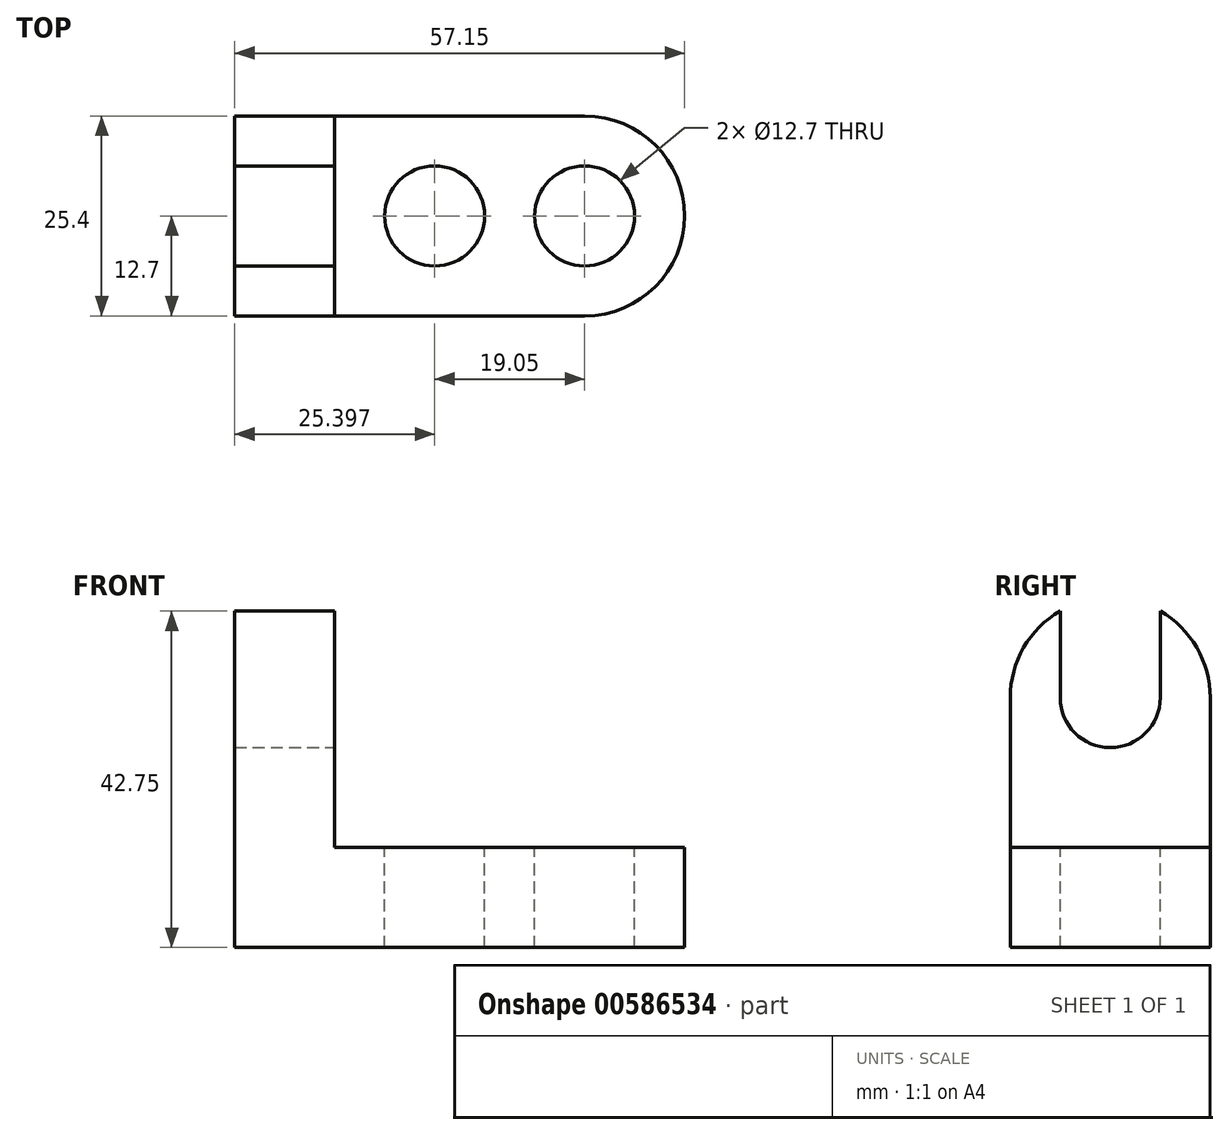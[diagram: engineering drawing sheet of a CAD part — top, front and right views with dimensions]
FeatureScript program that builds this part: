
annotation { "Feature Type Name" : "Feature", "Feature Type Description" : "" }
export const myFeature = defineFeature(function(context is Context, id is Id, definition is map)
    precondition{}
    {
        {
            var Q0;
            Q0=qCreatedBy(makeId("Front.planeOp"),FACE);
            var sketch = newSketch(context, id + "F0", { "sketchPlane" : qUnion([Q0])});
            skLineSegment(sketch, "E0", {"start": v(-66.14, 48.6) * mm, "end": v(-66.14, -2.2) * mm});
            skLineSegment(sketch, "E1", {"start": v(-66.14, -2.2) * mm, "end": v(-9, -2.2) * mm});
            skLineSegment(sketch, "E2", {"start": v(-9, -2.2) * mm, "end": v(-9, 10.5) * mm});
            skLineSegment(sketch, "E3", {"start": v(-9, 10.5) * mm, "end": v(-53.44, 10.5) * mm});
            skLineSegment(sketch, "E4", {"start": v(-53.44, 10.5) * mm, "end": v(-53.44, 48.6) * mm});
            skLineSegment(sketch, "E5", {"start": v(-53.44, 48.6) * mm, "end": v(-66.14, 48.6) * mm});
            skSolve(sketch);
        }
        {
            var Q0;
            Q0 = qSketchRegion(id + "F0", true);
            extrude(context, id + "F1", {"entities" : qUnion([Q0]), "depth" : 25.4 * mm, "offsetDistance" : 25.4 * mm});
        }
        {
            var Q0;
            Q0=makeQuery(id+"F1.opExtrude","SWEPT_FACE",FACE,{"disambiguationData":[OSD([sQuery(id+"F0.wireOp",EDGE,"E4")])]});
            var sketch = newSketch(context, id + "F2", { "sketchPlane" : qUnion([Q0])});
            skArc(sketch, "E6", {"start": v(0, 35.9) * mm, "mid": v(-12.7, 48.6) * mm, "end": v(-25.4, 35.9) * mm});
            skSolve(sketch);
        }
        {
            var Q0;
            Q0 = qSketchRegion(id + "F2", true);
            var Q1;
            {var subQ0=sQuery(id+"F2.wireOp",EDGE,"E6");var subQ1=sQuery(id+"F0.wireOp",EDGE,"E4");var subQ2=makeQuery(id+"F1.opExtrude","CAP_EDGE",EDGE,{"disambiguationData":[OSD([subQ1])],"isStart":false});var subQ3=makeQuery(id+"F2.imprint","INTERSECT",VERTEX,{"derivedFrom":[subQ2,subQ0]});Q1=makeQuery(id+"F2.imprint","IMPRINT",FACE,{"disambiguationData":[TD([[makeQuery(id+"F2.imprint","IMPRINT",EDGE,{"disambiguationData":[TD([[subQ3,1.0]])],"derivedFrom":subQ0}),-1.0]])]});}
            var Q2;
            {var subQ0=sQuery(id+"F2.wireOp",EDGE,"E6");var subQ1=sQuery(id+"F0.wireOp",EDGE,"E4");var subQ2=makeQuery(id+"F1.opExtrude","CAP_EDGE",EDGE,{"disambiguationData":[OSD([subQ1])],"isStart":true});var subQ3=makeQuery(id+"F2.imprint","INTERSECT",VERTEX,{"derivedFrom":[subQ2,subQ0]});Q2=makeQuery(id+"F2.imprint","IMPRINT",FACE,{"disambiguationData":[TD([[makeQuery(id+"F2.imprint","IMPRINT",EDGE,{"disambiguationData":[TD([[subQ3,-1.0]])],"derivedFrom":subQ0}),-1.0]])]});}
            extrude(context, id + "F3", {"entities" : qUnion([Q0, Q1, Q2]), "operationType" : NewBodyOperationType.REMOVE, "oppositeDirection" : true, "depth" : 25.4 * mm, "offsetDistance" : 25.4 * mm});
        }
        {
            var Q0;
            Q0=makeQuery(id+"F1.opExtrude","SWEPT_FACE",FACE,{"disambiguationData":[OSD([sQuery(id+"F0.wireOp",EDGE,"E4")])]});
            var sketch = newSketch(context, id + "F4", { "sketchPlane" : qUnion([Q0])});
            skArc(sketch, "E7", {"start": v(-19.05, 29.55) * mm, "mid": v(-12.7, 23.2) * mm, "end": v(-6.35, 29.55) * mm});
            skLineSegment(sketch, "E8", {"start": v(-19.05, 29.55) * mm, "end": v(-19.05, 46.9) * mm});
            skLineSegment(sketch, "E9", {"start": v(-6.35, 29.55) * mm, "end": v(-6.35, 46.9) * mm});
            skSolve(sketch);
        }
        {
            var Q0;
            Q0 = qSketchRegion(id + "F4", true);
            var Q1;
            Q1=makeQuery(id+"F4.imprint","IMPRINT",FACE,{"disambiguationData":[TD([[makeQuery(id+"F4.imprint","IMPRINT",EDGE,{"derivedFrom":sQuery(id+"F4.wireOp",EDGE,"E7")}),1.0]])]});
            extrude(context, id + "F5", {"entities" : qUnion([Q0, Q1]), "operationType" : NewBodyOperationType.REMOVE, "oppositeDirection" : true, "depth" : 25.4 * mm, "offsetDistance" : 25.4 * mm});
        }
        {
            var Q0;
            Q0=makeQuery(id+"F1.opExtrude","SWEPT_FACE",FACE,{"disambiguationData":[OSD([sQuery(id+"F0.wireOp",EDGE,"E3")])]});
            var sketch = newSketch(context, id + "F6", { "sketchPlane" : qUnion([Q0])});
            skCircle(sketch, "E10", {"center": v(-21.7, -12.7) * mm, "radius": 6.35 * mm});
            skCircle(sketch, "E11", {"center": v(-40.74, -12.7) * mm, "radius": 6.35 * mm});
            skSolve(sketch);
        }
        {
            var Q0;
            Q0 = qSketchRegion(id + "F6", true);
            extrude(context, id + "F7", {"entities" : qUnion([Q0]), "operationType" : NewBodyOperationType.REMOVE, "oppositeDirection" : true, "depth" : 25.4 * mm, "offsetDistance" : 25.4 * mm});
        }
        {
            var Q0;
            Q0=makeQuery(id+"F1.opExtrude","SWEPT_FACE",FACE,{"disambiguationData":[OSD([sQuery(id+"F0.wireOp",EDGE,"E3")])]});
            var sketch = newSketch(context, id + "F8", { "sketchPlane" : qUnion([Q0])});
            skArc(sketch, "E12", {"start": v(-21.7, -25.4) * mm, "mid": v(-9, -12.7) * mm, "end": v(-21.7, 0) * mm});
            skSolve(sketch);
        }
        {
            var Q0;
            Q0 = qSketchRegion(id + "F8", true);
            var Q1;
            {var subQ0=sQuery(id+"F8.wireOp",EDGE,"E12");var subQ1=sQuery(id+"F0.wireOp",EDGE,"E3");var subQ2=makeQuery(id+"F1.opExtrude","CAP_EDGE",EDGE,{"disambiguationData":[OSD([subQ1])],"isStart":true});var subQ3=makeQuery(id+"F8.imprint","INTERSECT",VERTEX,{"derivedFrom":[subQ2,subQ0]});Q1=makeQuery(id+"F8.imprint","IMPRINT",FACE,{"disambiguationData":[TD([[makeQuery(id+"F8.imprint","IMPRINT",EDGE,{"disambiguationData":[TD([[subQ3,1.0]])],"derivedFrom":subQ0}),-1.0]])]});}
            var Q2;
            {var subQ0=sQuery(id+"F8.wireOp",EDGE,"E12");var subQ1=sQuery(id+"F0.wireOp",EDGE,"E3");var subQ2=makeQuery(id+"F1.opExtrude","CAP_EDGE",EDGE,{"disambiguationData":[OSD([subQ1])],"isStart":false});var subQ3=makeQuery(id+"F8.imprint","INTERSECT",VERTEX,{"derivedFrom":[subQ2,subQ0]});Q2=makeQuery(id+"F8.imprint","IMPRINT",FACE,{"disambiguationData":[TD([[makeQuery(id+"F8.imprint","IMPRINT",EDGE,{"disambiguationData":[TD([[subQ3,-1.0]])],"derivedFrom":subQ0}),-1.0]])]});}
            extrude(context, id + "F9", {"entities" : qUnion([Q0, Q1, Q2]), "operationType" : NewBodyOperationType.REMOVE, "oppositeDirection" : true, "depth" : 25.4 * mm, "offsetDistance" : 25.4 * mm});
        }
        {
            var Q0;
            Q0=makeQuery(id+"F1.opExtrude","SWEPT_FACE",FACE,{"disambiguationData":[OSD([sQuery(id+"F0.wireOp",EDGE,"E4")])]});
            var sketch = newSketch(context, id + "F10", { "sketchPlane" : qUnion([Q0])});
            skArc(sketch, "E13", {"start": v(0, 29.55) * mm, "mid": v(-12.7, 42.25) * mm, "end": v(-25.4, 29.55) * mm});
            skSolve(sketch);
        }
        {
            var Q0;
            Q0 = qSketchRegion(id + "F10", true);
            var Q1;
            {var subQ0=sQuery(id+"F10.wireOp",EDGE,"E13");var subQ1=sQuery(id+"F0.wireOp",EDGE,"E4");var subQ2=makeQuery(id+"F1.opExtrude","CAP_EDGE",EDGE,{"disambiguationData":[OSD([subQ1])],"isStart":false});var subQ3=subQ2;var subQ4=makeQuery(id+"F10.imprint","INTERSECT",VERTEX,{"derivedFrom":[subQ3,subQ0]});Q1=makeQuery(id+"F10.imprint","IMPRINT",FACE,{"disambiguationData":[TD([[makeQuery(id+"F10.imprint","IMPRINT",EDGE,{"disambiguationData":[TD([[subQ4,1.0]])],"derivedFrom":subQ0}),-1.0]])]});}
            var Q2;
            {var subQ0=sQuery(id+"F10.wireOp",EDGE,"E13");var subQ1=sQuery(id+"F0.wireOp",EDGE,"E4");var subQ2=makeQuery(id+"F1.opExtrude","CAP_EDGE",EDGE,{"disambiguationData":[OSD([subQ1])],"isStart":true});var subQ3=subQ2;var subQ4=makeQuery(id+"F10.imprint","INTERSECT",VERTEX,{"derivedFrom":[subQ3,subQ0]});Q2=makeQuery(id+"F10.imprint","IMPRINT",FACE,{"disambiguationData":[TD([[makeQuery(id+"F10.imprint","IMPRINT",EDGE,{"disambiguationData":[TD([[subQ4,-1.0]])],"derivedFrom":subQ0}),-1.0]])]});}
            extrude(context, id + "F11", {"entities" : qUnion([Q0, Q1, Q2]), "operationType" : NewBodyOperationType.REMOVE, "oppositeDirection" : true, "depth" : 25.4 * mm, "offsetDistance" : 25.4 * mm});
        }
    });
